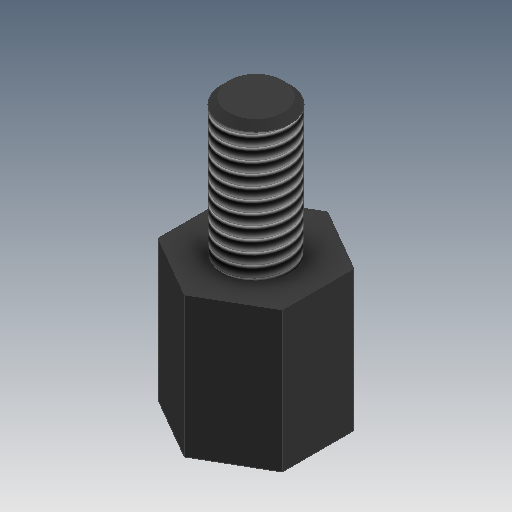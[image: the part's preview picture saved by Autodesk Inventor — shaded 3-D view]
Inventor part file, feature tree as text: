
AUTODESK INVENTOR PART (.ipt)
format: ipt  version: 2020 (Build 240168000, 168)  size: 146,432 bytes
history: native  units: in
note: dims shown in document units (in); Inventor stores cm internally (conversion verified against a paired STEP export)
features: extrude x3, sketch x3, thread x2, chamfer x2
ambient origin geometry x8: Origin, YZ Plane, XZ Plane, XY Plane, X Axis, Y Axis, Z Axis, Center Point
bodies: Solid1 (feature_tree)
feature tree (10):
  extrude  "Extrusion1"  Depth=0.2441in TaperAngle=0.0deg
  extrude  "Extrusion2"  Depth=0.2362in TaperAngle=0.0deg
  thread  "Thread1"  [1 undecoded]
  chamfer  "Chamfer1"  Distance=0.0118in Angle=45.0deg
  extrude  "Extrusion3"  Depth=0.1811in TaperAngle=0.0deg
  thread  "Thread2"  [1 undecoded]
  chamfer  "Chamfer2"  Distance=0.0118in Angle=45.0deg
  sketch  "Sketch1"  dims[d0=0.2157in d1=0.2441in d2=0.0in]
  sketch  "Sketch2"  dims[d3=0.1181in d4=0.2362in d5=0.0in d6=0.2362in d7=0.0in d8=0.0118in d9=0.0787in d10=45.0deg]
  sketch  "Sketch3"  dims[d11=0.1181in d12=0.1811in d13=0.0in d14=0.2756in d15=0.0in d16=0.0118in d17=0.0787in d18=45.0deg]
note: 2 required parameter values undecoded (feature->parameter linkage not recoverable at this tier; creation-order binding heuristic only, values carry confidence <= 0.55)
